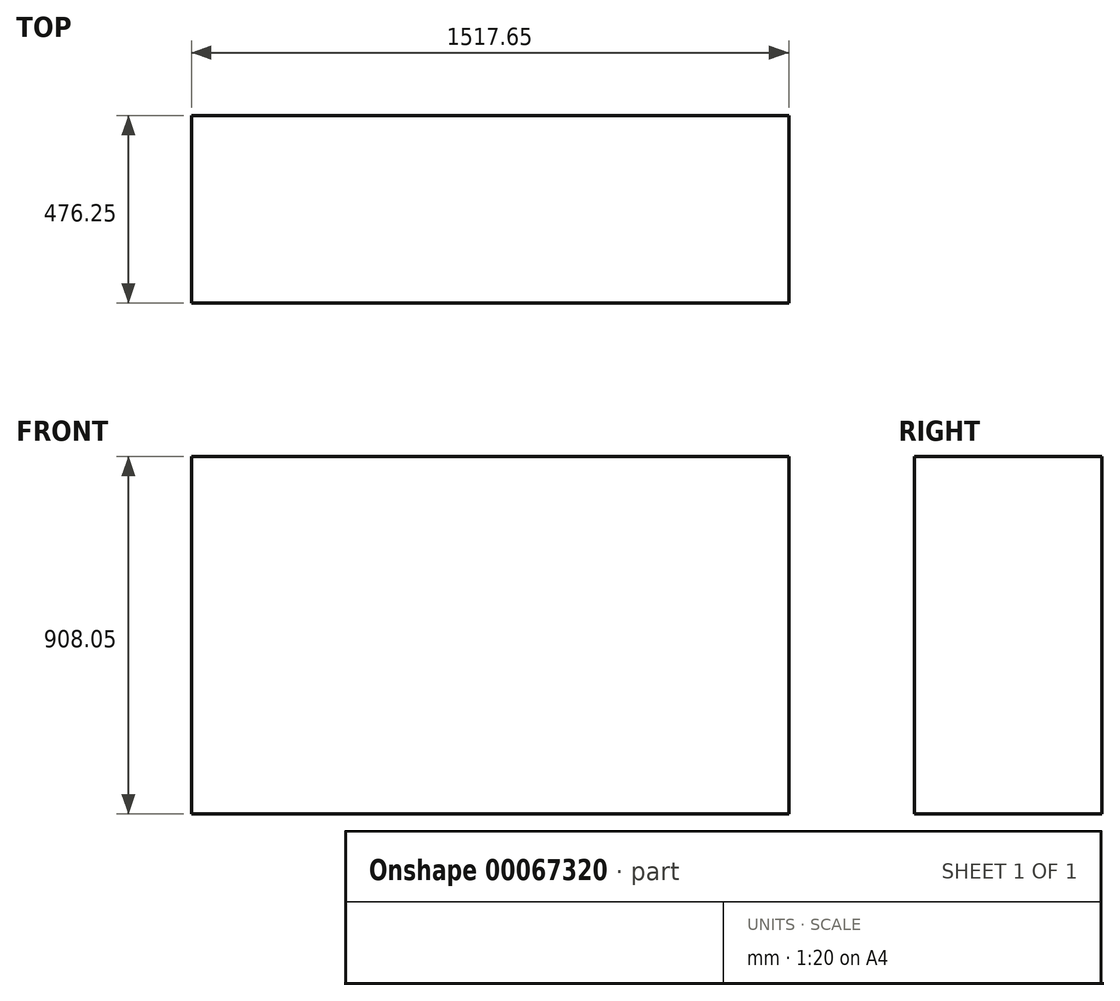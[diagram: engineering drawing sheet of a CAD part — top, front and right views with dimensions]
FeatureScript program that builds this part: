
annotation { "Feature Type Name" : "Feature", "Feature Type Description" : "" }
export const myFeature = defineFeature(function(context is Context, id is Id, definition is map)
    precondition{}
    {
        {
            var Q0;
            Q0=qCreatedBy(makeId("Top.planeOp"),FACE);
            var sketch = newSketch(context, id + "F0", { "sketchPlane" : qUnion([Q0])});
            skLineSegment(sketch, "E0.bottom", {"start": v(-753.46, 42.49) * mm, "end": v(764.2, 42.49) * mm});
            skLineSegment(sketch, "E0.top", {"start": v(-753.46, -433.76) * mm, "end": v(764.2, -433.76) * mm});
            skLineSegment(sketch, "E0.left", {"start": v(-753.46, 42.49) * mm, "end": v(-753.46, -433.76) * mm});
            skLineSegment(sketch, "E0.right", {"start": v(764.2, 42.49) * mm, "end": v(764.2, -433.76) * mm});
            skSolve(sketch);
        }
        {
            var Q0;
            Q0=makeQuery(id+"F0.imprint","IMPRINT",FACE,{"disambiguationData":[TD([[makeQuery(id+"F0.imprint","IMPRINT",EDGE,{"derivedFrom":sQuery(id+"F0.wireOp",EDGE,"E0.bottom")}),-1.0]])]});
            extrude(context, id + "F1", {"entities" : qUnion([Q0]), "depth" : 908.05 * mm});
        }
    });
